# Revit family: rba-bim-B824
name_source: partatom
category: Specialty Equipment
revit_build: Autodesk Revit 2018 (Build: 20170223_1515(x64)
units: mm (PartAtom-declared; Revit-internal decimal feet)

## family parameters
Cut with Voids When Loaded = No
Host = Face
OmniClass Number = 23.40.20.21
OmniClass Title = Toilet and Bath Specialties
Part Type = Normal
Room Calculation Point = No
Round Connector Dimension = Use Diameter
Shared = Yes

## types (7) — shared parameters
Assembly Depth = 1' - 4 5/8"
Bottle Depth = 0' - 10 3/8"
Bottle Dia = 0' - 3 7/8"
Capacity = 34 fl oz Soap
Fixture Material = Stainless Steel - Bobrick - Satin
Installation-Fabrication = http://www.bobrick.com
Keynote = 102813
Manufacturer Fax = 818-503-1930
Manufacturer Website = http://www.bobrick.com
Maximum Mounting Depth = 0' - 2"
Mounting Depth = 0' - 2"
Mounting Depth Location = 0' - 2"
Product Data = http://arcat.com
Recess Into Host = 0' - 4"
Revision = R1_10_2012
Sales Information = http://www.bobrick.com
Send Message = http://www.arcat.com
Spout Height = 0' - 2 15/16"
Spout Length = 0' - 6 3/4"
Spout Width = 0' - 2 3/4"
zero-valued in all types: Expected Lifespan (Years), Maintenance Schedule (Months), Warranty Duration (Years)

## per-type parameters (varying)
| type | Assembly Code | Default Elevation | Description | Manufacturer | Model | Modified Issue | URL |
| Foam Soap | E1090900 | 4' - 0" | Bobrick B-828 Counter Mounted Automatic Foam Soap Dispenser | Bobrick Washroom Equipment, Inc. | B-828 |  | http://www.bobrick.com |
| Liquid Soap | E1090900 | 4' - 0" | Counter Mounted Automatic Liquid Soap Dispenser | Bobrick Washroom Equipment, Inc. | B-824 | 20210812.01 | www.rba.com.au |
| B-823 | C1030210 | 0' - 0" | Bobrick Top-Fill Counter-Mounted Manual Foam Soap Dispenser | Bobrick Washroom Equipment, Inc | B-823 | 20210812.01 | http://www.rba.com.au |
| B-8226 | C1030210 | 4' - 0" | Lavatory-Mounted Soap Dispenser | RBA Group | B-8226 | 20161117.01 | www.rba.com.au |
| B-822 | C1030210 | 4' - 0" | Lavatory-Mounted Soap Dispenser | Bobrick Washroom Equipment, Inc. | B-Series | 20161117.01 | www.bobrick.com |
| B-8231 | C1030210 | 0' - 0" | Bobrick Top-Fill Counter-Mounted Manual Foam Soap Dispenser | Bobrick Washroom Equipment, Inc | B-8231 | 20161117.01 | http://www.rba.com.au |
| B-82216 | E1090900 | 4' - 0" | Bobrick B-82216 Lavatory Mounted Soap Dispenser | Bobrick Washroom Equipment, Inc. | B-82216 | 20161117.01 | http://www.bobrick.com |

## geometry (parser evidence)
native form markers: Blend x8, Sweep x1
no freeform markers — native parametric forms only
